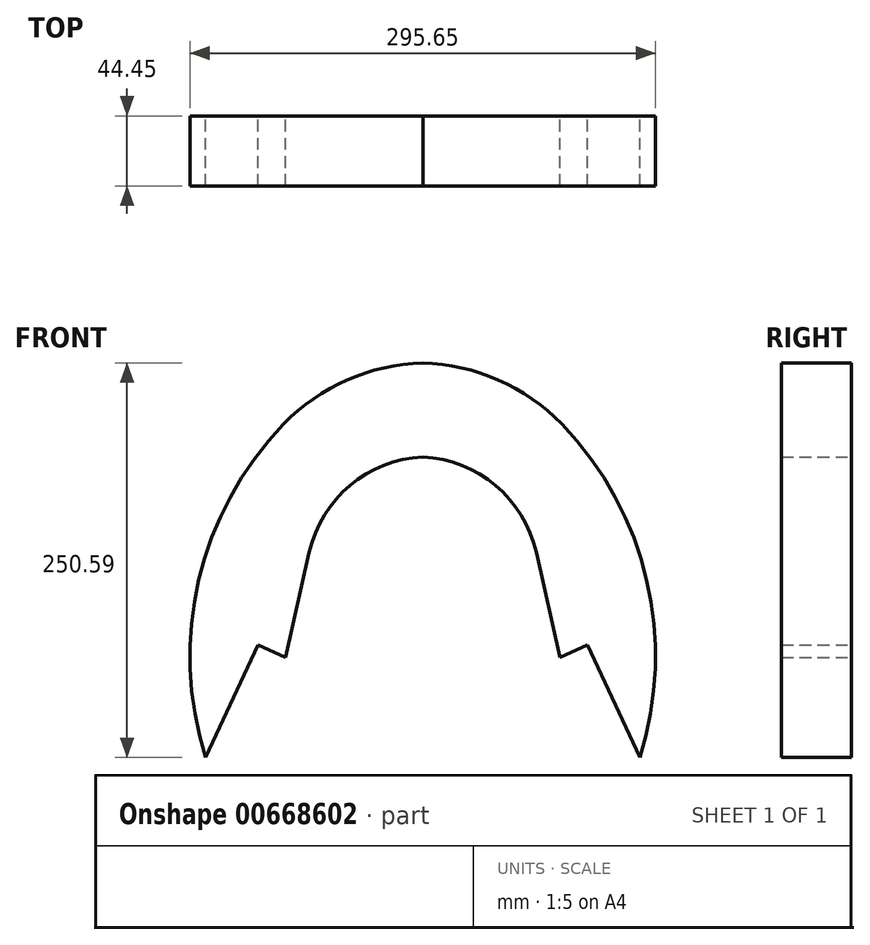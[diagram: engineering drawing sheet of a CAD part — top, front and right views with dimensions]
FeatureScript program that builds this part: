
annotation { "Feature Type Name" : "Feature", "Feature Type Description" : "" }
export const myFeature = defineFeature(function(context is Context, id is Id, definition is map)
    precondition{}
    {
        {
            var Q0;
            Q0=qCreatedBy(makeId("Front.planeOp"),FACE);
            var sketch = newSketch(context, id + "F0", { "sketchPlane" : qUnion([Q0])});
            skLineSegment(sketch, "E0", {"start": v(-139.4, -73.2) * mm, "end": v(-118.38, -28.03) * mm});
            skPoint(sketch, "E1.end.orphan", {"position": v(-118.38, -73.2) * mm});
            skPoint(sketch, "E2.start.orphan", {"position": v(97.52, -62.49) * mm});
            skLineSegment(sketch, "E3.trimOffspring", {"start": v(-151.68, -99.62) * mm, "end": v(-139.4, -73.2) * mm});
            skLineSegment(sketch, "E4", {"start": v(-118.38, -28.03) * mm, "end": v(-101.1, -36.06) * mm});
            skArc(sketch, "E5", {"start": v(-102.1, 112.15) * mm, "mid": v(-156.07, 13.1) * mm, "end": v(-151.68, -99.62) * mm});
            skArc(sketch, "E6", {"start": v(-13.83, 150.97) * mm, "mid": v(-61.77, 140.21) * mm, "end": v(-102.1, 112.15) * mm});
            skPoint(sketch, "E7.endSnap0", {"position": v(-13.83, 150.97) * mm});
            skLineSegment(sketch, "E8", {"start": v(-101.1, -36.06) * mm, "end": v(-85.96, 30.8) * mm});
            skArc(sketch, "E9", {"start": v(-13.83, 91.22) * mm, "mid": v(-60.09, 73.18) * mm, "end": v(-85.96, 30.8) * mm});
            skPoint(sketch, "E10.end.orphan", {"position": v(97.52, -17.32) * mm});
            skPoint(sketch, "E11.trimOffspring.start.orphan", {"position": v(130.81, -88.9) * mm});
            skArc(sketch, "E12.MirrorCS", {"start": v(-13.83, 150.97) * mm, "mid": v(34.1, 140.21) * mm, "end": v(74.44, 112.15) * mm});
            skArc(sketch, "E13.MirrorCS", {"start": v(74.44, 112.15) * mm, "mid": v(128.4, 13.1) * mm, "end": v(124.02, -99.62) * mm});
            skArc(sketch, "E14.MirrorCS", {"start": v(-13.83, 91.22) * mm, "mid": v(32.43, 73.18) * mm, "end": v(58.3, 30.8) * mm});
            skLineSegment(sketch, "E15.MirrorCS", {"start": v(73.45, -36.06) * mm, "end": v(58.3, 30.8) * mm});
            skLineSegment(sketch, "E16.MirrorCS", {"start": v(90.72, -28.03) * mm, "end": v(73.45, -36.06) * mm});
            skLineSegment(sketch, "E17.MirrorCS", {"start": v(111.73, -73.2) * mm, "end": v(90.72, -28.03) * mm});
            skLineSegment(sketch, "E18.MirrorCS", {"start": v(124.02, -99.62) * mm, "end": v(111.73, -73.2) * mm});
            skSolve(sketch);
        }
        {
            var Q0;
            Q0 = qSketchRegion(id + "F0", true);
            extrude(context, id + "F1", {"entities" : qUnion([Q0]), "depth" : 44.45 * mm, "offsetDistance" : 25.4 * mm});
        }
    });
